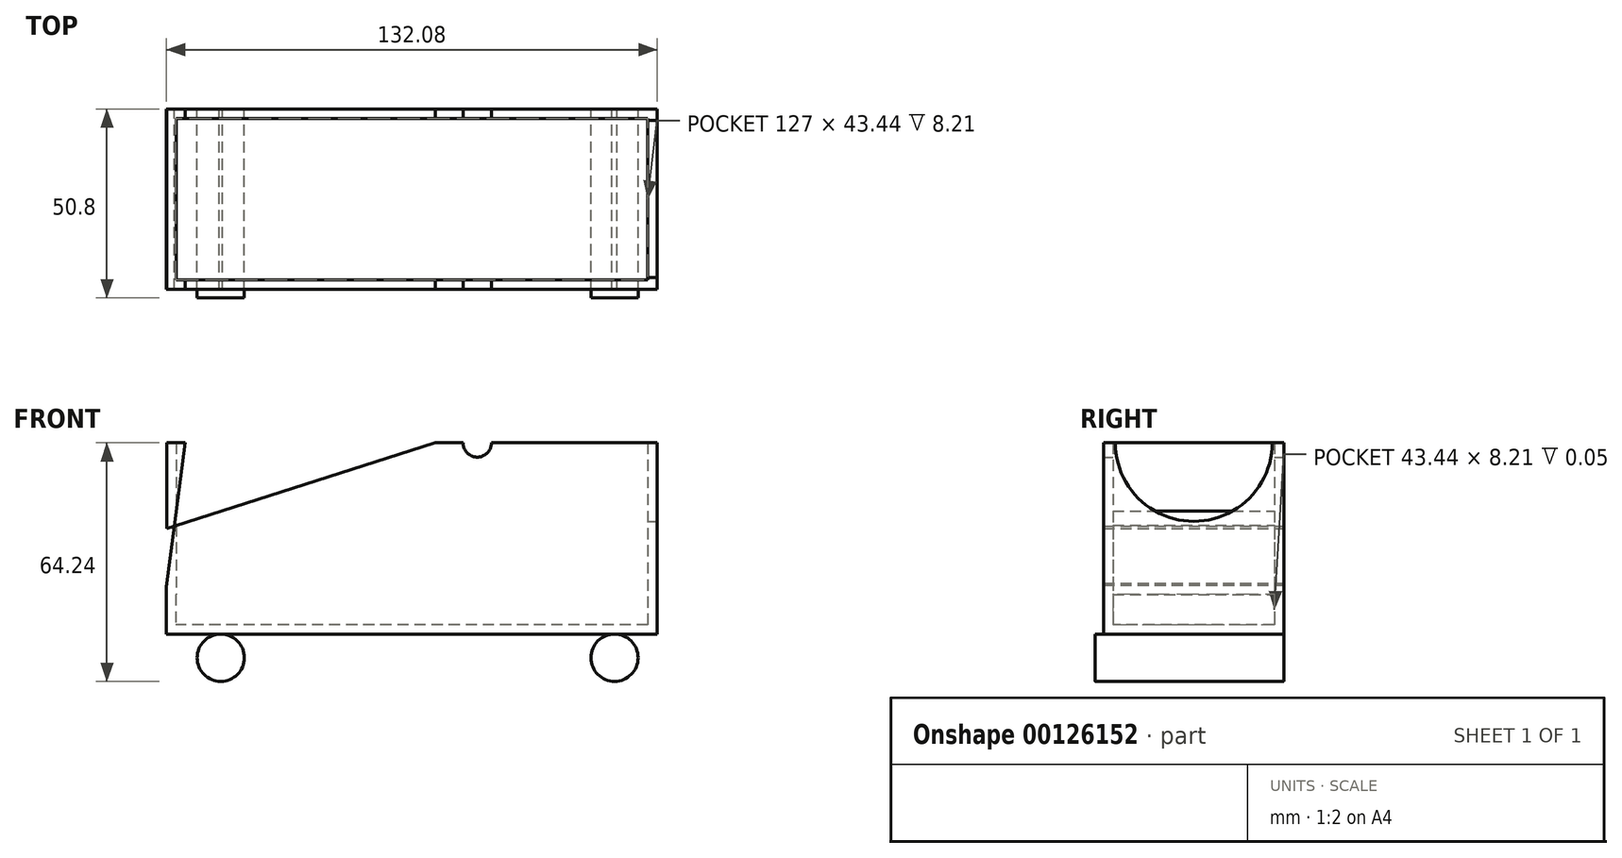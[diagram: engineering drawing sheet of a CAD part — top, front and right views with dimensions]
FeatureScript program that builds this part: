
annotation { "Feature Type Name" : "Feature", "Feature Type Description" : "" }
export const myFeature = defineFeature(function(context is Context, id is Id, definition is map)
    precondition{}
    {
        {
            var Q0;
            Q0=qCreatedBy(makeId("Right.planeOp"),FACE);
            var sketch = newSketch(context, id + "F0", { "sketchPlane" : qUnion([Q0])});
            skLineSegment(sketch, "E0.bottom", {"start": v(21.87, 0) * mm, "end": v(-26.65, 0) * mm});
            skLineSegment(sketch, "E0.top", {"start": v(21.87, -51.56) * mm, "end": v(-26.65, -51.56) * mm});
            skLineSegment(sketch, "E0.left", {"start": v(21.87, 0) * mm, "end": v(21.87, -51.56) * mm});
            skLineSegment(sketch, "E0.right", {"start": v(-26.65, 0) * mm, "end": v(-26.65, -51.56) * mm});
            skLineSegment(sketch, "E1.left", {"start": v(21.87, -24.97) * mm, "end": v(21.87, -51.56) * mm});
            skLineSegment(sketch, "E1.right", {"start": v(-26.65, -24.97) * mm, "end": v(-26.65, -51.56) * mm});
            skLineSegment(sketch, "E2", {"start": v(-26.65, -38.27) * mm, "end": v(21.87, -38.27) * mm});
            skSolve(sketch);
        }
        {
            var Q0;
            Q0=makeQuery(id+"F0.imprint","IMPRINT",FACE,{"disambiguationData":[TD([[makeQuery(id+"F0.imprint","IMPRINT",EDGE,{"derivedFrom":sQuery(id+"F0.wireOp",EDGE,"E0.bottom")}),1.0]])]});
            extrude(context, id + "F1", {"entities" : qUnion([Q0]), "depth" : 5.08 * mm});
        }
        {
            var Q0;
            Q0=makeQuery(id+"F0.imprint","IMPRINT",FACE,{"disambiguationData":[TD([[makeQuery(id+"F0.imprint","IMPRINT",EDGE,{"derivedFrom":sQuery(id+"F0.wireOp",EDGE,"E1.bottom")}),1.0]])]});
            var Q1;
            {var subQ0=sQuery(id+"F0.wireOp",EDGE,"E0.top");Q1=makeQuery(id+"F0.imprint","IMPRINT",FACE,{"disambiguationData":[TD([[makeQuery(id+"F0.imprint","IMPRINT",EDGE,{"derivedFrom":subQ0}),-1.0]])]});}
            extrude(context, id + "F2", {"entities" : qUnion([Q0, Q1]), "operationType" : NewBodyOperationType.ADD, "depth" : 5.08 * mm, "hasSecondDirection" : true, "secondDirectionOppositeDirection" : true, "secondDirectionDepth" : 127 * mm});
        }
        {
            var Q0;
            Q0=qCreatedBy(makeId("Front.planeOp"),FACE);
            var sketch = newSketch(context, id + "F3", { "sketchPlane" : qUnion([Q0])});
            skLineSegment(sketch, "E3", {"start": v(0, 0) * mm, "end": v(-54.61, 0) * mm});
            skLineSegment(sketch, "E4", {"start": v(-54.61, 0) * mm, "end": v(-214.05, -50.78) * mm});
            skLineSegment(sketch, "E5", {"start": v(0, 0) * mm, "end": v(0, -49.03) * mm});
            skLineSegment(sketch, "E6", {"start": v(0, -49.03) * mm, "end": v(-214.05, -50.78) * mm});
            skLineSegment(sketch, "E7", {"start": v(-54.61, 0) * mm, "end": v(-151.83, 0) * mm});
            skLineSegment(sketch, "E8", {"start": v(-151.83, 0) * mm, "end": v(-151.83, -38.22) * mm});
            skLineSegment(sketch, "E9", {"start": v(-127, -38.27) * mm, "end": v(-151.83, -38.22) * mm});
            skLineSegment(sketch, "E10", {"start": v(-127, -38.27) * mm, "end": v(-127, 0) * mm});
            skLineSegment(sketch, "E11", {"start": v(-127, 0) * mm, "end": v(-122, 0) * mm});
            skLineSegment(sketch, "E12", {"start": v(-122, 0) * mm, "end": v(-127, -38.27) * mm});
            skLineSegment(sketch, "E13", {"start": v(-125.58, -27.4) * mm, "end": v(-125.58, -38.27) * mm});
            skSolve(sketch);
        }
        {
            var Q0;
            Q0=makeQuery(id+"F0.imprint","IMPRINT",FACE,{"disambiguationData":[TD([[makeQuery(id+"F0.imprint","IMPRINT",EDGE,{"derivedFrom":sQuery(id+"F0.wireOp",EDGE,"E0.bottom")}),1.0]])]});
            extrude(context, id + "F4", {"entities" : qUnion([Q0]), "operationType" : NewBodyOperationType.ADD, "depth" : 0.26 * mm, "hasSecondDirection" : true, "secondDirectionOppositeDirection" : true, "secondDirectionDepth" : 126.95 * mm});
        }
        {
            var Q0;
            Q0=makeQuery(id+"F4.opExtrude","SWEPT_FACE",FACE,{"disambiguationData":[OSD([sQuery(id+"F3.wireOp",EDGE,"E4")])]});
            var Q1;
            Q1=makeQuery(id+"F4.boolean.opBoolean","MERGE",FACE,{"derivedFrom":[makeQuery(id+"F1.opExtrude","SWEPT_FACE",FACE,{"disambiguationData":[OSD([sQuery(id+"F0.wireOp",EDGE,"E0.bottom")])]}),makeQuery(id+"F4.opExtrude","SWEPT_FACE",FACE,{"disambiguationData":[OSD([sQuery(id+"F3.wireOp",EDGE,"E3")])]})]});
            shell(context, id + "F5", {"entities" : qUnion([Q0, Q1]), "thickness" : 2.54 * mm});
        }
        {
            var Q0;
            {var subQ0=sQuery(id+"F0.wireOp",EDGE,"E2");var subQ1=sQuery(id+"F0.wireOp",EDGE,"E1.right");var subQ2=sQuery(id+"F0.wireOp",EDGE,"E1.left");Q0=makeQuery(id+"F2.boolean.opBoolean","MERGE",FACE,{"derivedFrom":[makeQuery(id+"F1.opExtrude","CAP_FACE",FACE,{"disambiguationData":[OSD([sQuery(id+"F0.wireOp",EDGE,"E0.bottom"),sQuery(id+"F0.wireOp",EDGE,"E0.left"),sQuery(id+"F0.wireOp",EDGE,"E0.right"),subQ2,subQ1,subQ0])],"isStart":false}),makeQuery(id+"F2.opExtrude","CAP_FACE",FACE,{"disambiguationData":[OSD([sQuery(id+"F0.wireOp",EDGE,"E0.top"),subQ2,subQ1,subQ0])],"isStart":false})]});}
            var sketch = newSketch(context, id + "F6", { "sketchPlane" : qUnion([Q0])});
            skArc(sketch, "E14", {"start": v(-23.44, 0) * mm, "mid": v(-2.34, -21.15) * mm, "end": v(18.77, 0) * mm});
            skSolve(sketch);
        }
        {
            var Q0;
            Q0 = qSketchRegion(id + "F6", true);
            var Q1;
            {var subQ0=sQuery(id+"F6.wireOp",EDGE,"JrhRpI8L-slEY-GMoa-zQpC-F6i6lrFJm8nP");Q1=makeQuery(id+"F6.imprint","IMPRINT",FACE,{"disambiguationData":[TD([[makeQuery(id+"F6.imprint","IMPRINT",EDGE,{"derivedFrom":subQ0}),1.0]])]});}
            var Q2;
            {var subQ0=sQuery(id+"F6.wireOp",EDGE,"E14");Q2=makeQuery(id+"F6.imprint","IMPRINT",FACE,{"disambiguationData":[TD([[makeQuery(id+"F6.imprint","IMPRINT",EDGE,{"derivedFrom":subQ0}),1.0]])]});}
            extrude(context, id + "F7", {"entities" : qUnion([Q0, Q1, Q2]), "operationType" : NewBodyOperationType.REMOVE, "oppositeDirection" : true, "depth" : 25.4 * mm});
        }
        {
            var Q0;
            {var subQ0=sQuery(id+"F0.wireOp",EDGE,"E1.left");Q0=makeQuery(id+"F2.boolean.opBoolean","MERGE",FACE,{"derivedFrom":[makeQuery(id+"F1.opExtrude","SWEPT_FACE",FACE,{"disambiguationData":[OSD([sQuery(id+"F0.wireOp",EDGE,"E0.left"),subQ0])]}),makeQuery(id+"F2.opExtrude","SWEPT_FACE",FACE,{"disambiguationData":[OSD([subQ0])]})]});}
            var sketch = newSketch(context, id + "F8", { "sketchPlane" : qUnion([Q0])});
            skCircle(sketch, "E15", {"center": v(6.44, -57.87) * mm, "radius": 6.35 * mm});
            skCircle(sketch, "E16", {"center": v(112.38, -57.89) * mm, "radius": 6.35 * mm});
            skSolve(sketch);
        }
        {
            var Q0;
            Q0 = qSketchRegion(id + "F8", true);
            extrude(context, id + "F9", {"entities" : qUnion([Q0]), "operationType" : NewBodyOperationType.ADD, "oppositeDirection" : true, "depth" : 50.8 * mm});
        }
        {
            var Q0;
            {var subQ0=sQuery(id+"F3.wireOp",EDGE,"E7");Q0=makeQuery(id+"F3.imprint","IMPRINT",FACE,{"disambiguationData":[TD([[makeQuery(id+"F3.imprint","IMPRINT",EDGE,{"derivedFrom":subQ0}),1.0]])]});}
            var Q1;
            {var subQ5=sQuery(id+"F3.wireOp",EDGE,"E11");Q1=makeQuery(id+"F3.imprint","IMPRINT",FACE,{"disambiguationData":[TD([[makeQuery(id+"F3.imprint","IMPRINT",EDGE,{"derivedFrom":subQ5}),-1.0]])]});}
            var Q2;
            {var subQ0=sQuery(id+"F3.wireOp",EDGE,"E12");var subQ6=makeQuery(id+"F3.imprint","IMPRINT",VERTEX,{"derivedFrom":subQ0});Q2=makeQuery(id+"F3.imprint","IMPRINT",FACE,{"disambiguationData":[TD([[makeQuery(id+"F3.imprint","IMPRINT",EDGE,{"disambiguationData":[TD([[subQ6,1.0]])],"derivedFrom":subQ0}),-1.0]])]});}
            extrude(context, id + "F10", {"entities" : qUnion([Q0, Q1, Q2]), "operationType" : NewBodyOperationType.REMOVE, "depth" : 43.66 * mm, "hasSecondDirection" : true, "secondDirectionOppositeDirection" : true, "secondDirectionDepth" : 46.64 * mm});
        }
        {
            var Q0;
            {var subQ0=sQuery(id+"F0.wireOp",EDGE,"E1.left");var subQ1=sQuery(id+"F0.wireOp",EDGE,"E0.left");Q0=makeQuery(id+"F9.boolean.opBoolean","MERGE",FACE,{"derivedFrom":[makeQuery(id+"F4.boolean.opBoolean","MERGE",FACE,{"derivedFrom":[makeQuery(id+"F2.boolean.opBoolean","MERGE",FACE,{"derivedFrom":[makeQuery(id+"F1.opExtrude","SWEPT_FACE",FACE,{"disambiguationData":[OSD([subQ1,subQ0])]}),makeQuery(id+"F2.opExtrude","SWEPT_FACE",FACE,{"disambiguationData":[OSD([subQ0])]})]}),makeQuery(id+"F4.opExtrude","SWEPT_FACE",FACE,{"disambiguationData":[OSD([subQ1,subQ0])]})]}),makeQuery(id+"F9.opExtrude","CAP_FACE",FACE,{"disambiguationData":[OSD([sQuery(id+"F8.wireOp",EDGE,"E15")])],"isStart":true}),makeQuery(id+"F9.opExtrude","CAP_FACE",FACE,{"disambiguationData":[OSD([sQuery(id+"F8.wireOp",EDGE,"E16")])],"isStart":true})]});}
            var sketch = newSketch(context, id + "F11", { "sketchPlane" : qUnion([Q0])});
            skArc(sketch, "E17", {"start": v(39.56, 0) * mm, "mid": v(43.37, -3.87) * mm, "end": v(47.17, 0) * mm});
            skSolve(sketch);
        }
        {
            var Q0;
            {var subQ0=sQuery(id+"F11.wireOp",EDGE,"E17");Q0=makeQuery(id+"F11.imprint","IMPRINT",FACE,{"disambiguationData":[TD([[makeQuery(id+"F11.imprint","IMPRINT",EDGE,{"derivedFrom":subQ0}),1.0]])]});}
            extrude(context, id + "F12", {"entities" : qUnion([Q0]), "operationType" : NewBodyOperationType.REMOVE, "oppositeDirection" : true, "depth" : 67.9 * mm});
        }
    });
